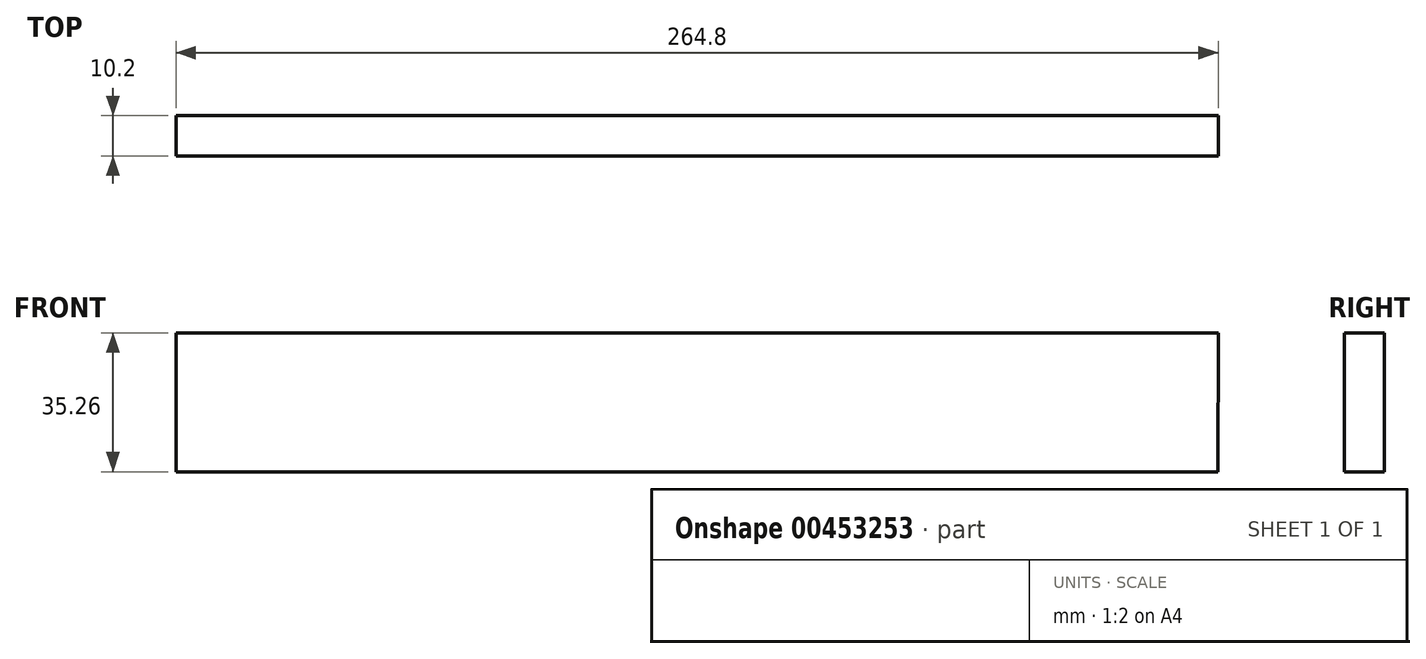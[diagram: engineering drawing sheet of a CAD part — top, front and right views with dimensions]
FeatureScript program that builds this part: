
annotation { "Feature Type Name" : "Feature", "Feature Type Description" : "" }
export const myFeature = defineFeature(function(context is Context, id is Id, definition is map)
    precondition{}
    {
        {
            var Q0;
            Q0=qCreatedBy(makeId("Front.planeOp"),FACE);
            var sketch = newSketch(context, id + "F0", { "sketchPlane" : qUnion([Q0])});
            skLineSegment(sketch, "E0", {"start": v(-133.1, 21.35) * mm, "end": v(-133.1, -13.9) * mm});
            skLineSegment(sketch, "E1", {"start": v(-133.1, -13.9) * mm, "end": v(131.58, -13.9) * mm});
            skLineSegment(sketch, "E2", {"start": v(-133.1, 21.35) * mm, "end": v(131.7, 21.35) * mm});
            skLineSegment(sketch, "E3", {"start": v(131.7, 21.35) * mm, "end": v(131.58, -13.9) * mm});
            skSolve(sketch);
        }
        {
            var Q0;
            Q0 = qSketchRegion(id + "F0", true);
            extrude(context, id + "F1", {"entities" : qUnion([Q0]), "depth" : 10.2 * mm});
        }
    });
